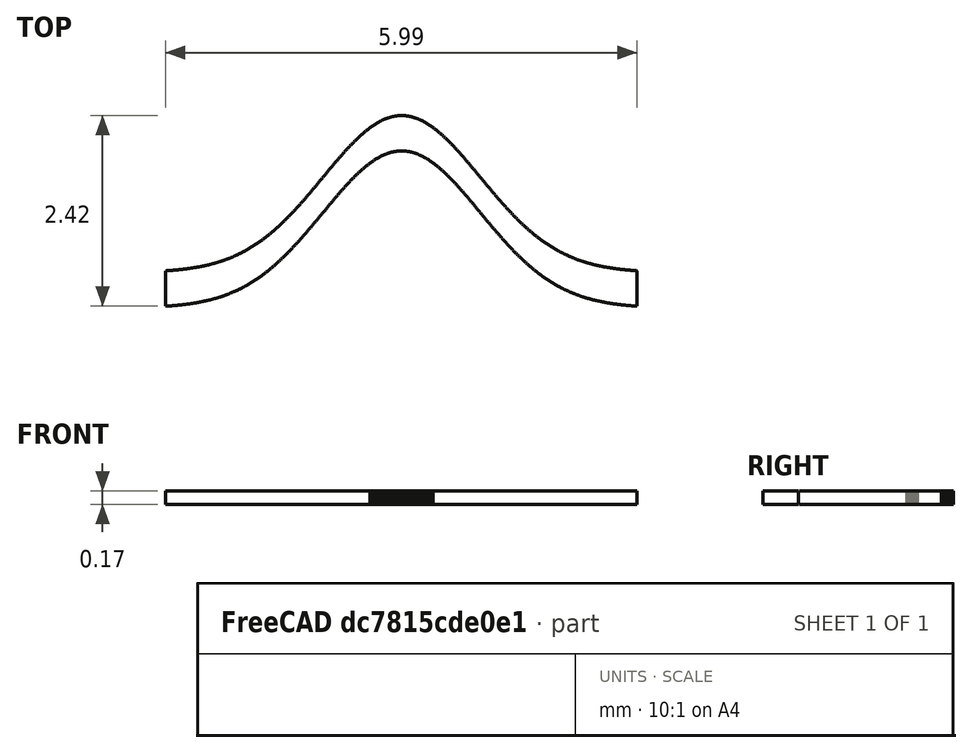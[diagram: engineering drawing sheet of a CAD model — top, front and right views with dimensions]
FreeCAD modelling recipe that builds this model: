
FCSTD DOCUMENT  (FreeCAD 0.19R23141 (Git))
Label: bornal
License: All rights reserved
LicenseURL: http://en.wikipedia.org/wiki/All_rights_reserved
objects: Sketcher::SketchObject×2, Part::Feature×1, PartDesign::AdditivePipe×1, PartDesign::Body×1
note: 6 computed .brp shape members not serialized (recipe doc carries the construction recipe); baked Part::Feature solids carry a one-line shape summary decoded from their .brp

FEATURE [Sketcher::SketchObject] Sketch
  MapMode = 5
  Placement = pos=(0,0,0) rot=(0.57735,0.57735,0.57735;2.0944rad)
  sketch-geometry (4):
    g0: LineSegment StartX=0 StartY=0 StartZ=0 EndX=1.2656e-11 EndY=0 EndZ=0
    g1: LineSegment StartX=1.2656e-11 StartY=0 StartZ=0 EndX=1.2656e-11 EndY=1.84134 EndZ=0
    g2: LineSegment StartX=1.2656e-11 StartY=1.84134 StartZ=0 EndX=0 EndY=1.84134 EndZ=0
    g3: LineSegment StartX=0 StartY=1.84134 StartZ=0 EndX=0 EndY=0 EndZ=0
  constraints (10):
    c: Coincident(g0,g1)
    c: Coincident(g1,g2)
    c: Coincident(g2,g3)
    c: Coincident(g3,g0)
    c: Horizontal(g0)
    c: Horizontal(g2)
    c: Vertical(g1)
    c: Vertical(g3)
    c: Coincident(g0,g-1)
    c: PointOnObject(g1,g-2)
FEATURE [Sketcher::SketchObject] Sketch001
  MapMode = 5
  Placement = pos=(0,0,0) rot=(0.57735,0.57735,0.57735;2.0944rad)
  Support = -> [YZ_Plane]
  sketch-geometry (4):
    g0: LineSegment StartX=0 StartY=0 StartZ=0 EndX=0.449654 EndY=0 EndZ=0
    g1: LineSegment StartX=0.449654 StartY=0 StartZ=0 EndX=0.449654 EndY=0.172056 EndZ=0
    g2: LineSegment StartX=0.449654 StartY=0.172056 StartZ=0 EndX=0 EndY=0.172056 EndZ=0
    g3: LineSegment StartX=0 StartY=0.172056 StartZ=0 EndX=0 EndY=0 EndZ=0
  constraints (9):
    c: Coincident(g0,g1)
    c: Coincident(g1,g2)
    c: Coincident(g2,g3)
    c: Coincident(g3,g0)
    c: Horizontal(g0)
    c: Horizontal(g2)
    c: Vertical(g1)
    c: Vertical(g3)
    c: Coincident(g0,g-1)
FEATURE [Part::Feature] Shape
  shape: bbox 5.99 x 1.973 x 2e-07 mm, 0 faces, 0 solids (baked)
FEATURE [PartDesign::AdditivePipe] AdditivePipe
  AuxilleryCurvelinear = true
  AuxillerySpineTangent = false
  Binormal = (0,0,0)
  Mode = 0
  Placement = pos=(0,0,0) rot=(0.57735,0.57735,0.57735;2.0944rad)
  Profile = -> Sketch001
  Refine = true
  Spine = -> Shape
  SpineTangent = false
  Transformation = 0
  Transition = 0
FEATURE [PartDesign::Body] Body
  Group = -> [Sketch001,AdditivePipe]
  Origin = -> Origin
  Tip = -> AdditivePipe
